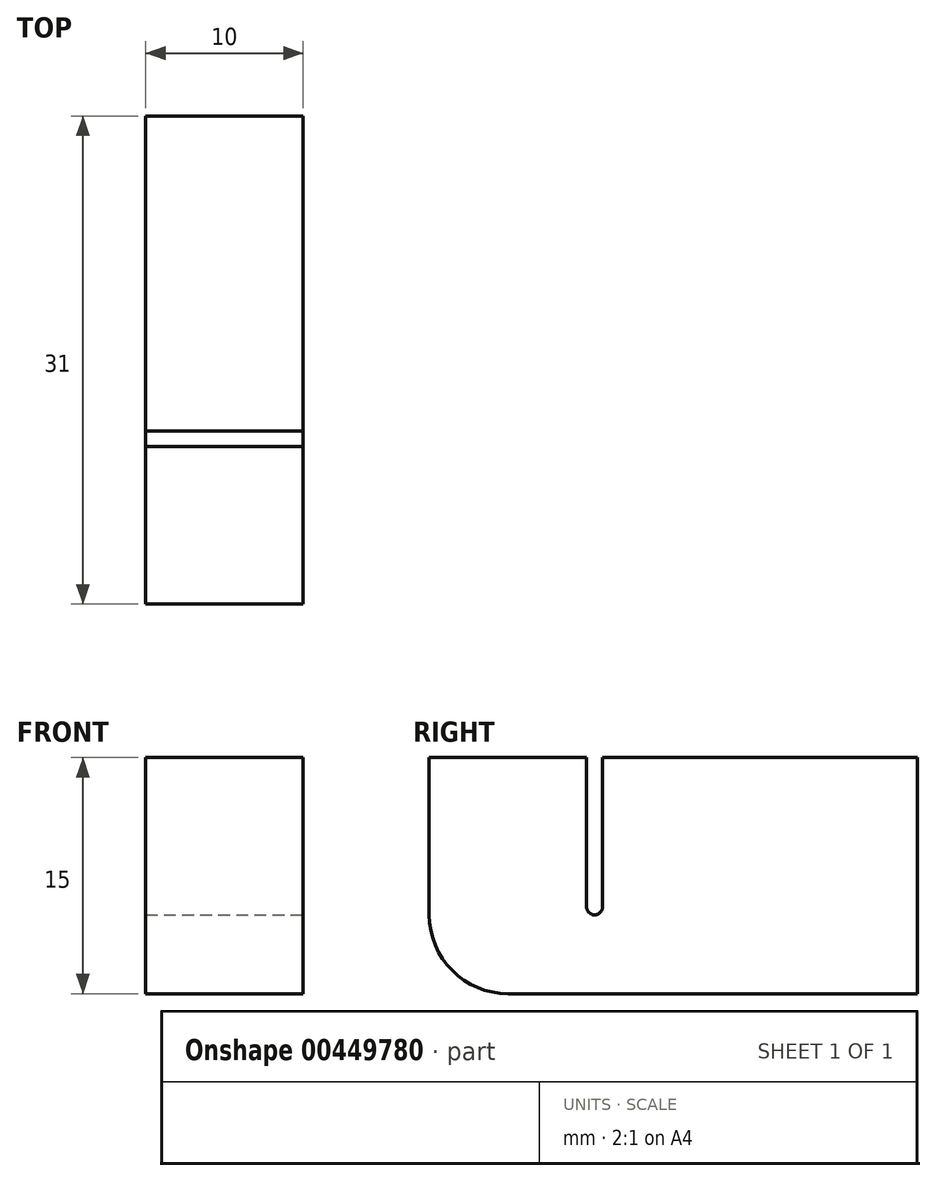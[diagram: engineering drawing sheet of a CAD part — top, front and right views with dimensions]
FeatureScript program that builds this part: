
annotation { "Feature Type Name" : "Feature", "Feature Type Description" : "" }
export const myFeature = defineFeature(function(context is Context, id is Id, definition is map)
    precondition{}
    {
        {
            var Q0;
            Q0=qCreatedBy(makeId("Right.planeOp"),FACE);
            var sketch = newSketch(context, id + "F0", { "sketchPlane" : qUnion([Q0])});
            skLineSegment(sketch, "E0.bottom", {"start": v(20, 10) * mm, "end": v(0, 10) * mm});
            skLineSegment(sketch, "E0.top", {"start": v(20, -5) * mm, "end": v(0, -5) * mm});
            skLineSegment(sketch, "E0.left", {"start": v(20, 10) * mm, "end": v(20, -5) * mm});
            skLineSegment(sketch, "E0.right", {"start": v(0, 10) * mm, "end": v(0, -5) * mm});
            skLineSegment(sketch, "E1.bottom", {"start": v(0, -5) * mm, "end": v(-1, -5) * mm});
            skLineSegment(sketch, "E1.top", {"start": v(0, 0) * mm, "end": v(-1, 0) * mm});
            skLineSegment(sketch, "E1.left", {"start": v(0, -5) * mm, "end": v(0, 0) * mm});
            skLineSegment(sketch, "E1.right", {"start": v(-1, -5) * mm, "end": v(-1, 0) * mm});
            skLineSegment(sketch, "E2.bottom", {"start": v(-1, -5) * mm, "end": v(-6, -5) * mm});
            skLineSegment(sketch, "E2.top", {"start": v(-1, 10) * mm, "end": v(-11, 10) * mm});
            skLineSegment(sketch, "E2.left", {"start": v(-1, -5) * mm, "end": v(-1, 10) * mm});
            skLineSegment(sketch, "E2.right", {"start": v(-11, 0) * mm, "end": v(-11, 10) * mm});
            skPoint(sketch, "E3.visualSharp", {"position": v(-11, -5) * mm});
            skArc(sketch, "E3.filletArc", {"start": v(-11, 0) * mm, "mid": v(-9.54, -3.54) * mm, "end": v(-6, -5) * mm});
            skSolve(sketch);
        }
        {
            var Q0;
            Q0 = qSketchRegion(id + "F0", true);
            extrude(context, id + "F1", {"entities" : qUnion([Q0]), "depth" : 10 * mm});
        }
        {
            var Q0;
            Q0=makeQuery(id+"F1.opExtrude","SWEPT_EDGE",EDGE,{"disambiguationData":[OSD([sQuery(id+"F0.wireOp",EDGE,"E0.right"),sQuery(id+"F0.wireOp",EDGE,"E1.top"),sQuery(id+"F0.wireOp",EDGE,"E1.left")])]});
            var Q1;
            Q1=makeQuery(id+"F1.opExtrude","SWEPT_EDGE",EDGE,{"disambiguationData":[OSD([sQuery(id+"F0.wireOp",EDGE,"E1.top"),sQuery(id+"F0.wireOp",EDGE,"E2.left")])]});
            fillet(context, id + "F2", {"entities" : qUnion([Q0, Q1]), "radius" : 0.5 * mm, "tangentPropagation" : true, "allowEdgeOverflow" : false});
        }
    });
